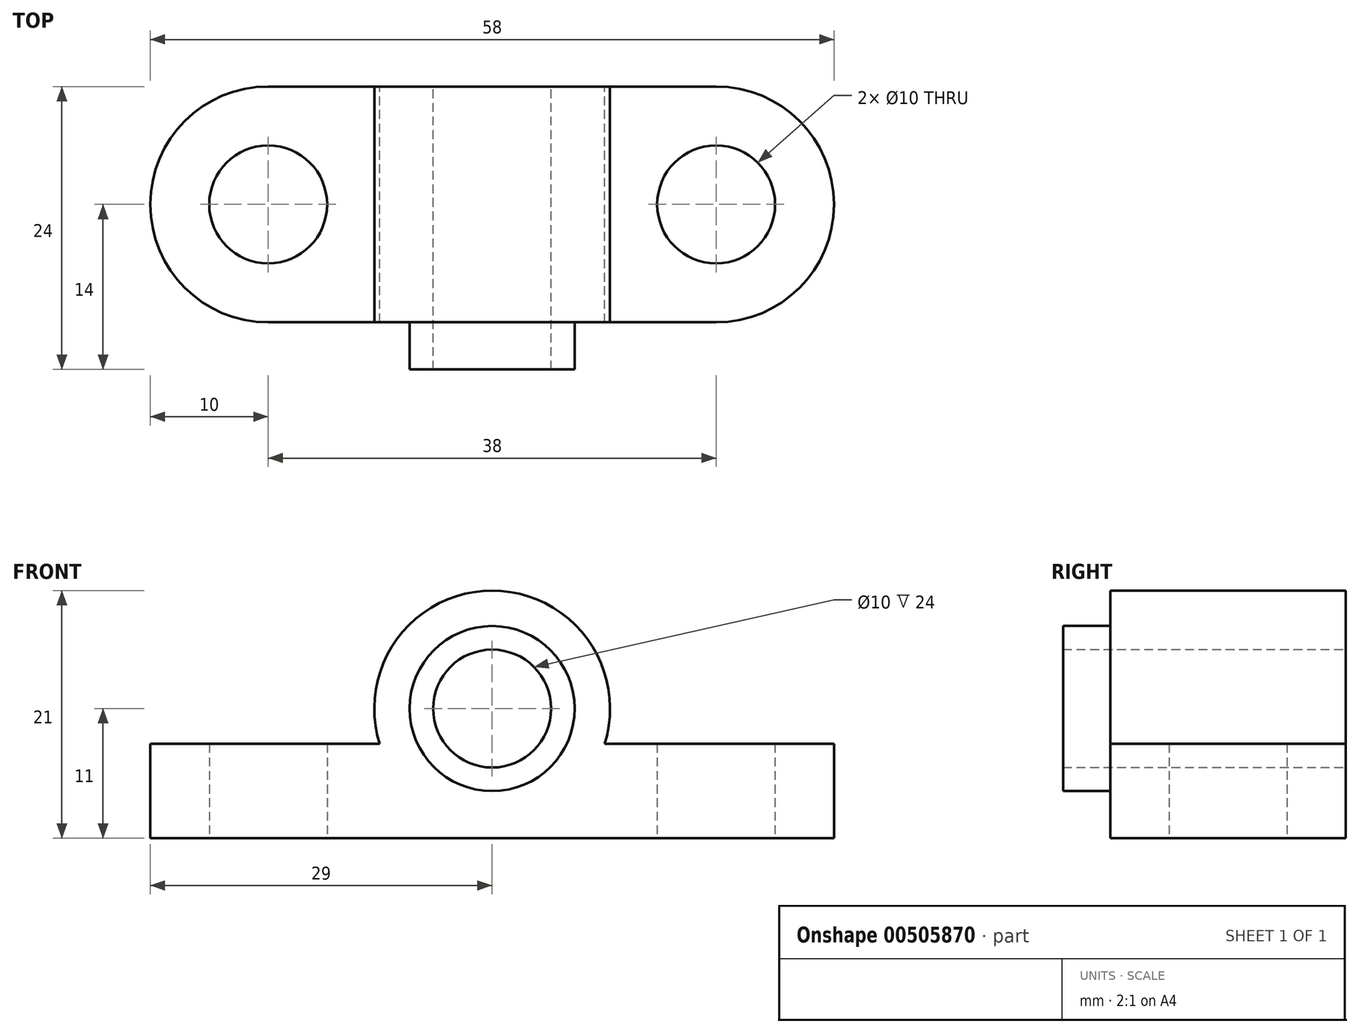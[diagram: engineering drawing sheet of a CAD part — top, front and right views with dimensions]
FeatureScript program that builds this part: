
annotation { "Feature Type Name" : "Feature", "Feature Type Description" : "" }
export const myFeature = defineFeature(function(context is Context, id is Id, definition is map)
    precondition{}
    {
        {
            var Q0;
            Q0=qCreatedBy(makeId("Top.planeOp"),FACE);
            var sketch = newSketch(context, id + "F0", { "sketchPlane" : qUnion([Q0])});
            skLineSegment(sketch, "E0", {"start": v(0, 0) * mm, "end": v(19, 0) * mm});
            skLineSegment(sketch, "E1", {"start": v(19, 0) * mm, "end": v(19, -20) * mm, "construction": true});
            skLineSegment(sketch, "E2", {"start": v(19, -20) * mm, "end": v(0, -20) * mm});
            skLineSegment(sketch, "E3", {"start": v(0, -20) * mm, "end": v(0, 0) * mm, "construction": true});
            skArc(sketch, "E4", {"start": v(19, -20) * mm, "mid": v(29, -10) * mm, "end": v(19, 0) * mm});
            skCircle(sketch, "E5", {"center": v(19, -10) * mm, "radius": 5 * mm});
            skArc(sketch, "E6.MirrorCS", {"start": v(-19, -20) * mm, "mid": v(-29, -10) * mm, "end": v(-19, 0) * mm});
            skCircle(sketch, "E7.MirrorC", {"center": v(-19, -10) * mm, "radius": 5 * mm});
            skLineSegment(sketch, "E8.MirrorCS", {"start": v(0, 0) * mm, "end": v(-19, 0) * mm});
            skLineSegment(sketch, "E9.MirrorCS", {"start": v(-19, -20) * mm, "end": v(0, -20) * mm});
            skLineSegment(sketch, "E10.MirrorCS", {"start": v(-19, 0) * mm, "end": v(-19, -20) * mm, "construction": true});
            skSolve(sketch);
        }
        {
            var Q0;
            Q0=makeQuery(id+"F0.imprint","IMPRINT",FACE,{"disambiguationData":[TD([[makeQuery(id+"F0.imprint","IMPRINT",EDGE,{"derivedFrom":sQuery(id+"F0.wireOp",EDGE,"E0")}),-1.0]])]});
            extrude(context, id + "F1", {"entities" : qUnion([Q0]), "depth" : 8 * mm});
        }
        {
            var Q0;
            Q0=qCreatedBy(makeId("Front.planeOp"),FACE);
            var sketch = newSketch(context, id + "F2", { "sketchPlane" : qUnion([Q0])});
            skLineSegment(sketch, "E11", {"start": v(0, 0) * mm, "end": v(0, 11) * mm, "construction": true});
            skCircle(sketch, "E12", {"center": v(0, 11) * mm, "radius": 5 * mm});
            skCircle(sketch, "E13", {"center": v(0, 11) * mm, "radius": 7 * mm});
            skCircle(sketch, "E14", {"center": v(0, 11) * mm, "radius": 10 * mm});
            skLineSegment(sketch, "E15", {"start": v(-10, 11) * mm, "end": v(-10, 0) * mm});
            skLineSegment(sketch, "E16", {"start": v(10, 11) * mm, "end": v(10, 0) * mm});
            skSolve(sketch);
        }
        {
            var Q0;
            Q0=makeQuery(id+"F2.imprint","IMPRINT",FACE,{"disambiguationData":[TD([[makeQuery(id+"F2.imprint","IMPRINT",EDGE,{"derivedFrom":sQuery(id+"F2.wireOp",EDGE,"E13")}),-1.0]])]});
            extrude(context, id + "F3", {"entities" : qUnion([Q0]), "operationType" : NewBodyOperationType.ADD, "depth" : 20 * mm});
        }
        {
            var Q0;
            Q0=makeQuery(id+"F2.imprint","IMPRINT",FACE,{"disambiguationData":[TD([[makeQuery(id+"F2.imprint","IMPRINT",EDGE,{"derivedFrom":sQuery(id+"F2.wireOp",EDGE,"E12")}),-1.0]])]});
            extrude(context, id + "F4", {"entities" : qUnion([Q0]), "operationType" : NewBodyOperationType.ADD, "depth" : 24 * mm});
        }
        {
            var Q0;
            Q0=sQuery(id+"F2.wireOp",VERTEX,"E12.center");
            var Q1;
            Q1=makeQuery(id+"F1.opExtrude","SWEPT_BODY",BODY,{"disambiguationData":[OSD([sQuery(id+"F0.wireOp",EDGE,"E0"),sQuery(id+"F0.wireOp",EDGE,"E2"),sQuery(id+"F0.wireOp",EDGE,"E4"),sQuery(id+"F0.wireOp",EDGE,"E5"),sQuery(id+"F0.wireOp",EDGE,"E6.MirrorCS"),sQuery(id+"F0.wireOp",EDGE,"E7.MirrorC"),sQuery(id+"F0.wireOp",EDGE,"E8.MirrorCS"),sQuery(id+"F0.wireOp",EDGE,"E9.MirrorCS")])]});
            hole(context, id + "F5", {"style" : HoleStyle.SIMPLE, "endStyle" : HoleEndStyle.BLIND, "oppositeDirection" : true, "holeDiameter" : 10 * mm, "holeDepth" : 20 * mm, "isTappedThrough" : true, "tappedDepth" : 12 * mm, "tapClearance" : 3, "locations" : qUnion([Q0]), "scope" : qUnion([Q1])});
        }
    });
